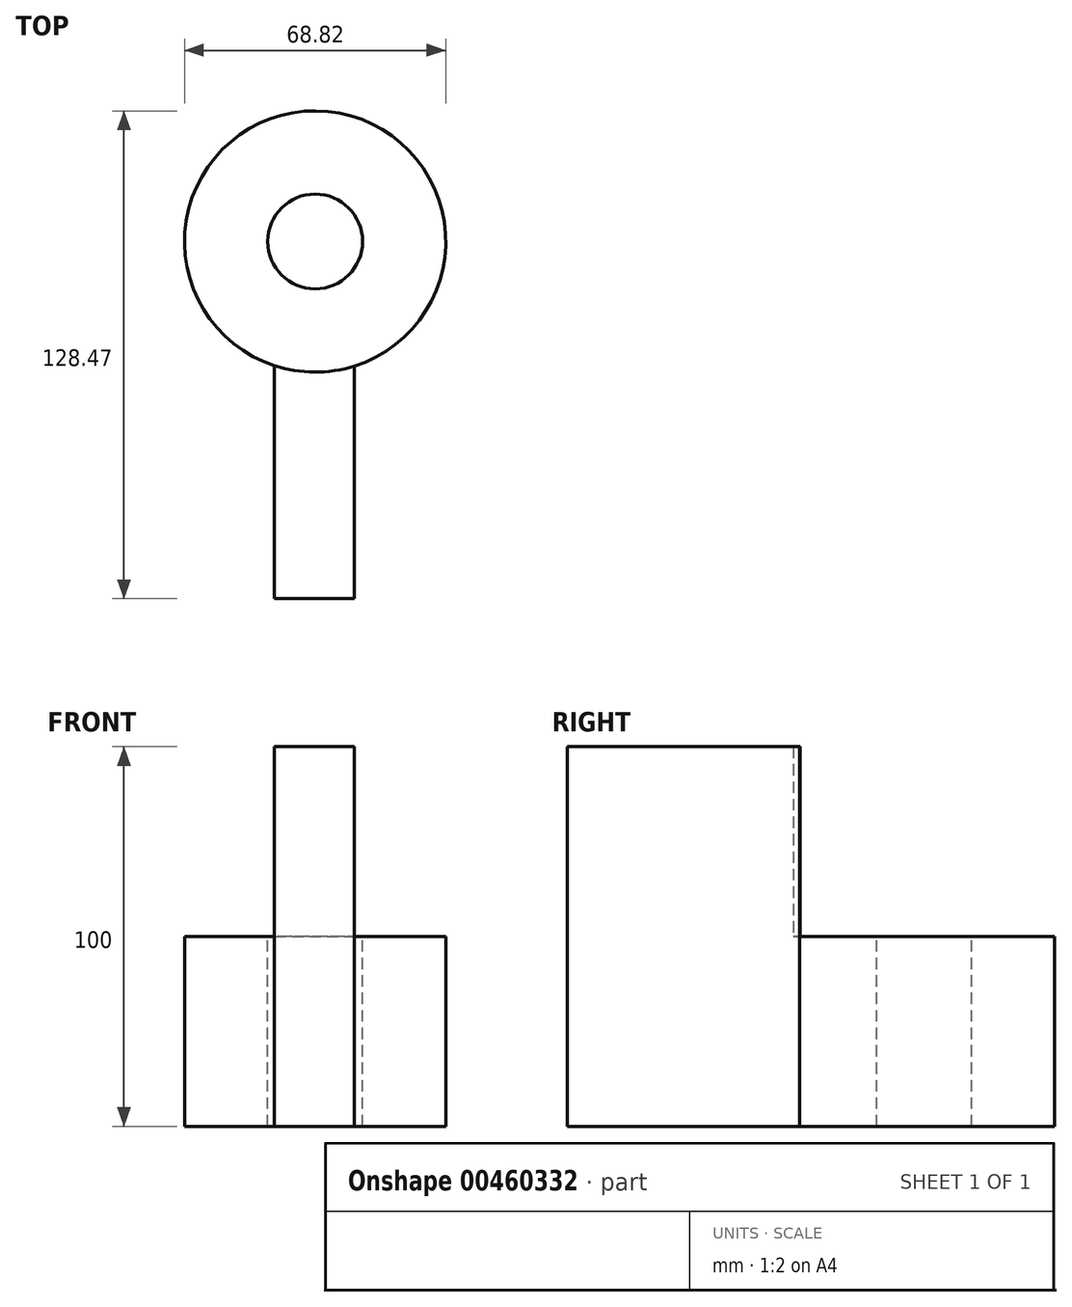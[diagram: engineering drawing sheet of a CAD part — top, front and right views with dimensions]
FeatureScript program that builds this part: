
annotation { "Feature Type Name" : "Feature", "Feature Type Description" : "" }
export const myFeature = defineFeature(function(context is Context, id is Id, definition is map)
    precondition{}
    {
        {
            var Q0;
            Q0=qCreatedBy(makeId("Top.planeOp"),FACE);
            var sketch = newSketch(context, id + "F0", { "sketchPlane" : qUnion([Q0])});
            skCircle(sketch, "E0", {"center": v(-38.13, 32.84) * mm, "radius": 34.41 * mm});
            skLineSegment(sketch, "E1", {"start": v(-38.13, 32.84) * mm, "end": v(-38.13, -61.23) * mm, "construction": true});
            skLineSegment(sketch, "E2", {"start": v(-48.82, 0.13) * mm, "end": v(-48.82, -61.22) * mm});
            skLineSegment(sketch, "E3", {"start": v(-48.82, -61.22) * mm, "end": v(-27.85, -61.22) * mm});
            skLineSegment(sketch, "E4", {"start": v(-27.85, -61.22) * mm, "end": v(-27.85, 0) * mm});
            skSolve(sketch);
        }
        {
            var Q0;
            {var subQ0=sQuery(id+"F0.wireOp",EDGE,"E0");var subQ1=makeQuery(id+"F0.imprint","INTERSECT",VERTEX,{"derivedFrom":[subQ0,sQuery(id+"F0.wireOp",EDGE,"E2")]});Q0=makeQuery(id+"F0.imprint","IMPRINT",FACE,{"disambiguationData":[TD([[makeQuery(id+"F0.imprint","IMPRINT",EDGE,{"disambiguationData":[TD([[subQ1,-1.0]])],"derivedFrom":subQ0}),1.0]])]});}
            extrude(context, id + "F1", {"entities" : qUnion([Q0]), "depth" : 50 * mm});
        }
        {
            var Q0;
            {var subQ0=sQuery(id+"F0.wireOp",EDGE,"E2");Q0=makeQuery(id+"F0.imprint","IMPRINT",FACE,{"disambiguationData":[TD([[makeQuery(id+"F0.imprint","IMPRINT",EDGE,{"derivedFrom":subQ0}),1.0]])]});}
            extrude(context, id + "F2", {"entities" : qUnion([Q0]), "operationType" : NewBodyOperationType.ADD, "depth" : 100 * mm});
        }
        {
            var Q0;
            Q0=makeQuery(id+"F1.opExtrude","CAP_FACE",FACE,{"disambiguationData":[OSD([sQuery(id+"F0.wireOp",EDGE,"E0")])],"isStart":false});
            var sketch = newSketch(context, id + "F3", { "sketchPlane" : qUnion([Q0])});
            skCircle(sketch, "E5", {"center": v(-38.13, 32.84) * mm, "radius": 12.5 * mm});
            skSolve(sketch);
        }
        {
            var Q0;
            Q0=makeQuery(id+"F3.imprint","IMPRINT",FACE,{"disambiguationData":[TD([[makeQuery(id+"F3.imprint","IMPRINT",EDGE,{"derivedFrom":sQuery(id+"F3.wireOp",EDGE,"E5")}),1.0]])]});
            extrude(context, id + "F4", {"entities" : qUnion([Q0]), "operationType" : NewBodyOperationType.REMOVE, "oppositeDirection" : true, "depth" : 100 * mm});
        }
    });
